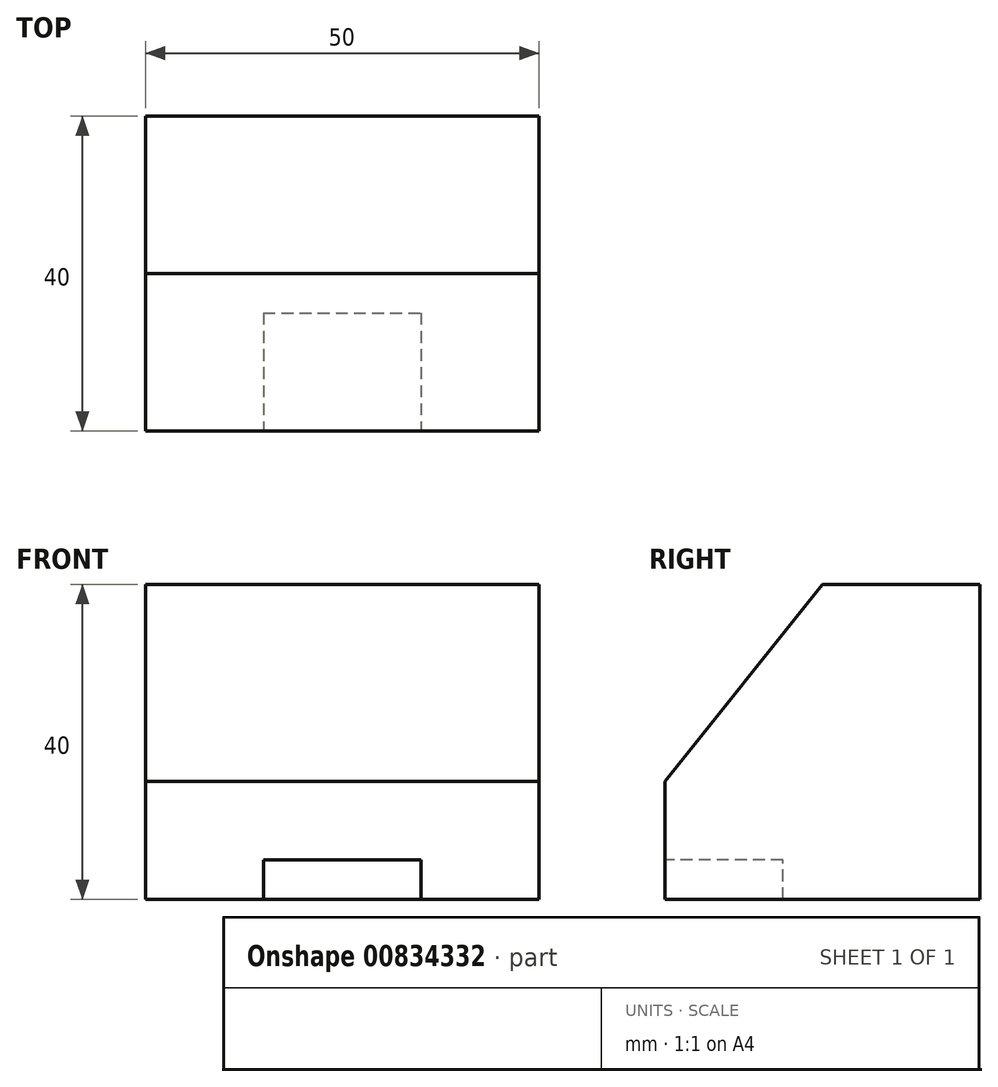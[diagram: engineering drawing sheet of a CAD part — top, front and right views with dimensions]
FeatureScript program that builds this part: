
annotation { "Feature Type Name" : "Feature", "Feature Type Description" : "" }
export const myFeature = defineFeature(function(context is Context, id is Id, definition is map)
    precondition{}
    {
        {
            var Q0;
            Q0=qCreatedBy(makeId("Right.planeOp"),FACE);
            var sketch = newSketch(context, id + "F0", { "sketchPlane" : qUnion([Q0])});
            skLineSegment(sketch, "E0", {"start": v(-20, 40) * mm, "end": v(0, 40) * mm});
            skLineSegment(sketch, "E1", {"start": v(0, 40) * mm, "end": v(0, 0) * mm});
            skLineSegment(sketch, "E2", {"start": v(0, 0) * mm, "end": v(-40, 0) * mm});
            skLineSegment(sketch, "E3", {"start": v(-40, 0) * mm, "end": v(-40, 15) * mm});
            skLineSegment(sketch, "E4", {"start": v(-40, 15) * mm, "end": v(-20, 40) * mm});
            skSolve(sketch);
        }
        {
            var Q0;
            Q0 = qSketchRegion(id + "F0", true);
            extrude(context, id + "F1", {"entities" : qUnion([Q0]), "oppositeDirection" : true, "depth" : 50 * mm, "offsetDistance" : 25 * mm});
        }
        {
            var Q0;
            Q0=makeQuery(id+"F1.opExtrude","SWEPT_FACE",FACE,{"disambiguationData":[OSD([sQuery(id+"F0.wireOp",EDGE,"E3")])]});
            var sketch = newSketch(context, id + "F2", { "sketchPlane" : qUnion([Q0])});
            skLineSegment(sketch, "E5.bottom", {"start": v(-35, 0) * mm, "end": v(-15, 0) * mm});
            skLineSegment(sketch, "E5.top", {"start": v(-35, 5) * mm, "end": v(-15, 5) * mm});
            skLineSegment(sketch, "E5.left", {"start": v(-35, 0) * mm, "end": v(-35, 5) * mm});
            skLineSegment(sketch, "E5.right", {"start": v(-15, 0) * mm, "end": v(-15, 5) * mm});
            skSolve(sketch);
        }
        {
            var Q0;
            Q0=makeQuery(id+"F2.imprint","IMPRINT",FACE,{"disambiguationData":[TD([[makeQuery(id+"F2.imprint","IMPRINT",EDGE,{"derivedFrom":sQuery(id+"F2.wireOp",EDGE,"E5.bottom")}),1.0]])]});
            extrude(context, id + "F3", {"entities" : qUnion([Q0]), "operationType" : NewBodyOperationType.REMOVE, "oppositeDirection" : true, "depth" : 15 * mm, "offsetDistance" : 25 * mm});
        }
    });
